# Revit family: Sink-Corian-European-Spicy-967
name_source: partatom
category: Plumbing Fixtures
revit_build: Autodesk Revit 2015 (Build: 20140606_1530(x64)
units: mm (PartAtom-declared; Revit-internal decimal feet)

## types (1)
- 967
    CWFU = 0
    Cost = 0 $
    Default Elevation = 1219 mm
    Depth = 155 mm  [stored 0.50853 ft]
    Description = Kitchen Sink Europe Specification
    Finish = Solid Surface Sink - DuPont - Bone
    HWFU = 0
    Interior Depth = 140 mm  [stored 0.459318 ft]
    Interior Length = 350 mm  [stored 1.14829 ft]
    Interior Width = 160 mm  [stored 0.524934 ft]
    Length = 401 mm  [stored 1.31562 ft]
    Manufacturer = DuPont
    Model = Spicy 967
    Product Page URL = http://www.corian.uk
    Sink Colors Available = Bone, Cameo White, Designer White, Glacier White, Vanilla
    URL = http://www.corian.uk
    Version = 2015 - v1.0a
    WFU = 0
    Width = 211 mm  [stored 0.692257 ft]

note: [stored X ft] marks values corroborated as IEEE doubles in the binary element streams (Revit-internal decimal feet)

## geometry (parser evidence)
native form markers: Sweep x2
no freeform markers — native parametric forms only
